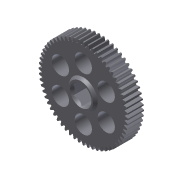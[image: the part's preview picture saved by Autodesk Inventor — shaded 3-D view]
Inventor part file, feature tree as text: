
AUTODESK INVENTOR PART (.ipt)
format: ipt  version: 2013 (Build 170138000, 138)  size: 472,064 bytes
history: native  units: mm (DEFAULTED — no unit token found)
features: sketch x6, extrude x4, plane x3, other x3, revolve x1, pattern_circular x1, projected_geometry x1
ambient origin geometry x8: Origin, YZ Plane, XZ Plane, XY Plane, X Axis, Y Axis, Z Axis, Center Point
bodies: Solid1 (feature_tree)
feature tree (19):
  extrude  "Extrusion1"  Depth=8.763mm TaperAngle=0.0deg
  plane  "Work Plane1"
  plane  "Work Plane2"
  plane  "Work Plane3"
  other  "Spur Gear"
  extrude  "Extrusion2"  Depth=76.2mm TaperAngle=0.0deg
  extrude  "Extrusion3"  TaperAngle=0.0deg  [1 undecoded]
  revolve  "Revolution1"  [1 undecoded]
  extrude  "Extrusion4"  Depth=1.397mm TaperAngle=0.0deg
  pattern_circular  "Circular Pattern1"  [2 undecoded]
  sketch  "Sketch1"  dims[d0=49.2125mm d1=8.763mm d2=0.0mm]
  sketch  "Sketch2"  dims[d3=47.625mm d4=76.2mm d5=0.0mm]
  other  "Srf1"
  sketch  "Sketch3"  dims[d6=0.0mm d7=0.523599mm d9=0.0mm]
  sketch  "Sketch4"  dims[d20=15.875mm d21=1.397mm d22=0.0mm]
  sketch  "Sketch5"  dims[d23=9.525mm d24=1.397mm d25=0.0mm]
  sketch  "Sketch6"  dims[d26=1.143mm d27=0.889mm d28=8.850565mm d29=90.0deg d30=9.525mm d31=14.605mm d32=1.397mm d33=0.0mm d34=60.0mm d35=360.0deg]
  other  "Pitch Diameter"
  projected_geometry  "Project Cut Edges1"
note: 4 required parameter values undecoded (feature->parameter linkage not recoverable at this tier; creation-order binding heuristic only, values carry confidence <= 0.55)